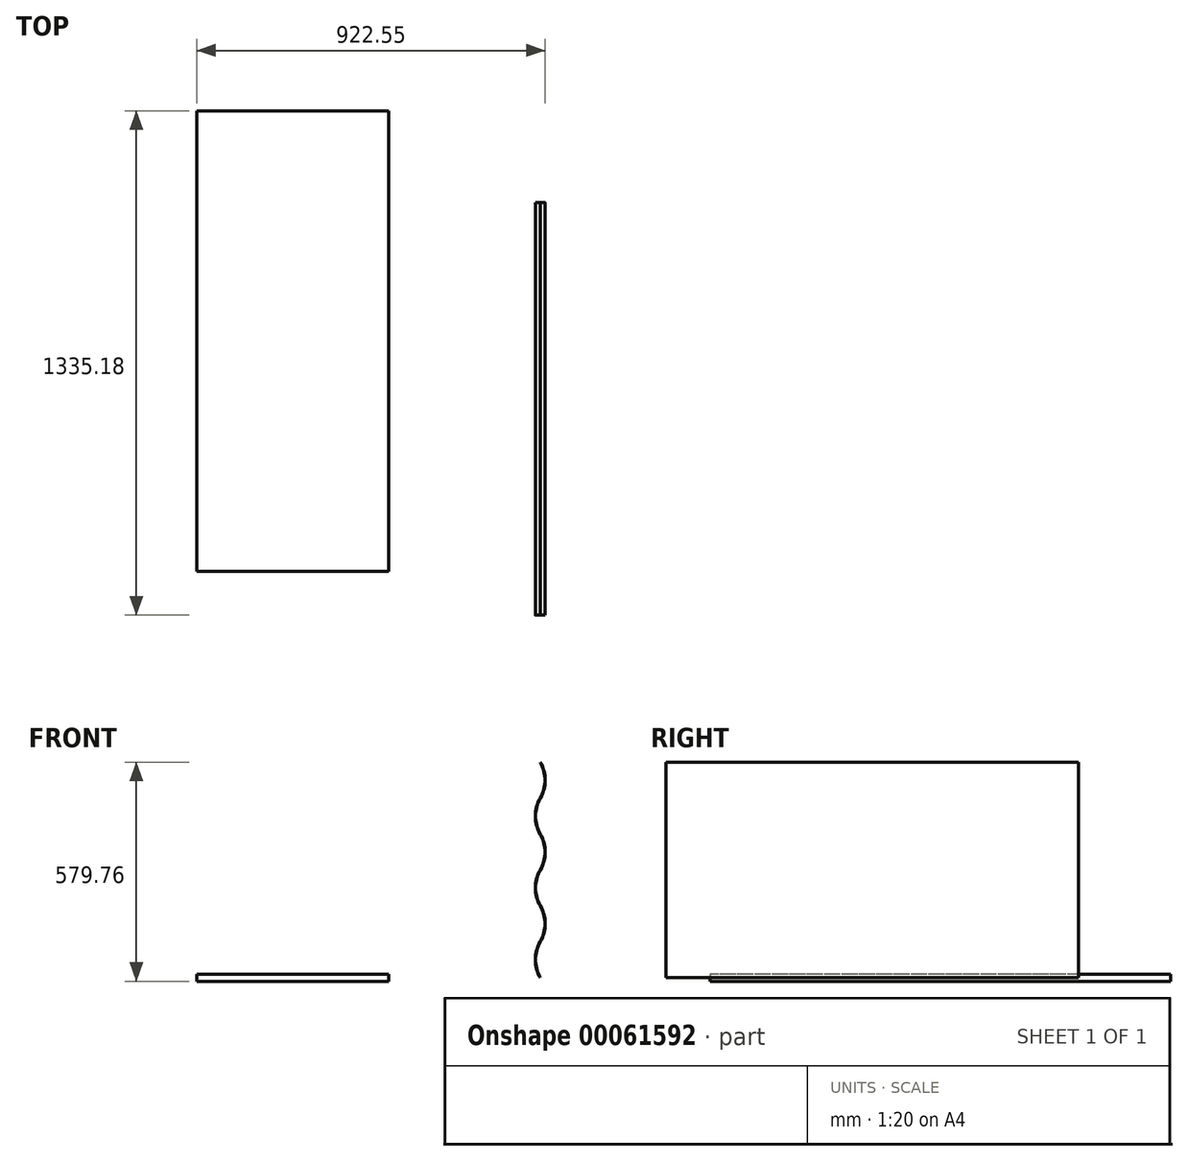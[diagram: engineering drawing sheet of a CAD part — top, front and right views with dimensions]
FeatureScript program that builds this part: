
annotation { "Feature Type Name" : "Feature", "Feature Type Description" : "" }
export const myFeature = defineFeature(function(context is Context, id is Id, definition is map)
    precondition{}
    {
        {
            var Q0;
            Q0=qCreatedBy(makeId("Front.planeOp"),FACE);
            var sketch = newSketch(context, id + "F0", { "sketchPlane" : qUnion([Q0])});
            skArc(sketch, "E0", {"start": v(0, 95.04) * mm, "mid": v(-12.7, 47.52) * mm, "end": v(0, 0) * mm});
            skArc(sketch, "E1", {"start": v(0, 95.04) * mm, "mid": v(12.7, 142.56) * mm, "end": v(0, 190.08) * mm});
            skArc(sketch, "E2", {"start": v(0, 285.11) * mm, "mid": v(-12.7, 237.6) * mm, "end": v(0, 190.08) * mm});
            skArc(sketch, "E3", {"start": v(0, 285.11) * mm, "mid": v(12.7, 332.63) * mm, "end": v(0, 380.15) * mm});
            skArc(sketch, "E4", {"start": v(0, 475.2) * mm, "mid": v(-12.7, 427.67) * mm, "end": v(0, 380.15) * mm});
            skArc(sketch, "E5", {"start": v(0, 475.2) * mm, "mid": v(12.7, 522.7) * mm, "end": v(0, 570.23) * mm});
            skArc(sketch, "E6.1.0.0", {"start": v(0.76, 475.2) * mm, "mid": v(13.46, 522.7) * mm, "end": v(0.76, 570.23) * mm});
            skArc(sketch, "E6.1.0.1", {"start": v(0.76, 285.11) * mm, "mid": v(13.46, 332.63) * mm, "end": v(0.76, 380.15) * mm});
            skArc(sketch, "E6.1.0.2", {"start": v(0.76, 475.2) * mm, "mid": v(-11.94, 427.67) * mm, "end": v(0.76, 380.15) * mm});
            skArc(sketch, "E6.1.0.3", {"start": v(0.76, 285.11) * mm, "mid": v(-11.94, 237.6) * mm, "end": v(0.76, 190.08) * mm});
            skArc(sketch, "E6.1.0.4", {"start": v(0.76, 95.04) * mm, "mid": v(13.46, 142.56) * mm, "end": v(0.76, 190.08) * mm});
            skArc(sketch, "E6.1.0.5", {"start": v(0.76, 95.04) * mm, "mid": v(-11.94, 47.52) * mm, "end": v(0.76, 0) * mm});
            skLineSegment(sketch, "E6.direction1", {"start": v(-82.55, 522.7) * mm, "end": v(-81.79, 522.7) * mm, "construction": true});
            skLineSegment(sketch, "E7", {"start": v(0, 570.23) * mm, "end": v(0.76, 570.23) * mm});
            skLineSegment(sketch, "E8", {"start": v(0, 0) * mm, "end": v(0.76, 0) * mm});
            skSolve(sketch);
        }
        {
            var Q0;
            Q0=makeQuery(id+"F0.imprint","IMPRINT",FACE,{"disambiguationData":[TD([[makeQuery(id+"F0.imprint","IMPRINT",EDGE,{"derivedFrom":sQuery(id+"F0.wireOp",EDGE,"E0")}),1.0]])]});
            extrude(context, id + "F1", {"entities" : qUnion([Q0]), "endBound" : BoundingType.SYMMETRIC, "depth" : 1092.2 * mm});
        }
        {
            var Q0;
            Q0=qCreatedBy(makeId("Top.planeOp"),FACE);
            var sketch = newSketch(context, id + "F2", { "sketchPlane" : qUnion([Q0])});
            skLineSegment(sketch, "E9.bottom", {"start": v(-909.09, 789.08) * mm, "end": v(-401.09, 789.08) * mm});
            skLineSegment(sketch, "E9.top", {"start": v(-909.09, -430.12) * mm, "end": v(-401.09, -430.12) * mm});
            skLineSegment(sketch, "E9.left", {"start": v(-909.09, 789.08) * mm, "end": v(-909.09, -430.12) * mm});
            skLineSegment(sketch, "E9.right", {"start": v(-401.09, 789.08) * mm, "end": v(-401.09, -430.12) * mm});
            skSolve(sketch);
        }
        {
            var Q0;
            Q0=makeQuery(id+"F2.imprint","IMPRINT",FACE,{"disambiguationData":[TD([[makeQuery(id+"F2.imprint","IMPRINT",EDGE,{"derivedFrom":sQuery(id+"F2.wireOp",EDGE,"E9.bottom")}),-1.0]])]});
            extrude(context, id + "F3", {"entities" : qUnion([Q0]), "endBound" : BoundingType.SYMMETRIC, "depth" : 19.05 * mm});
        }
    });
